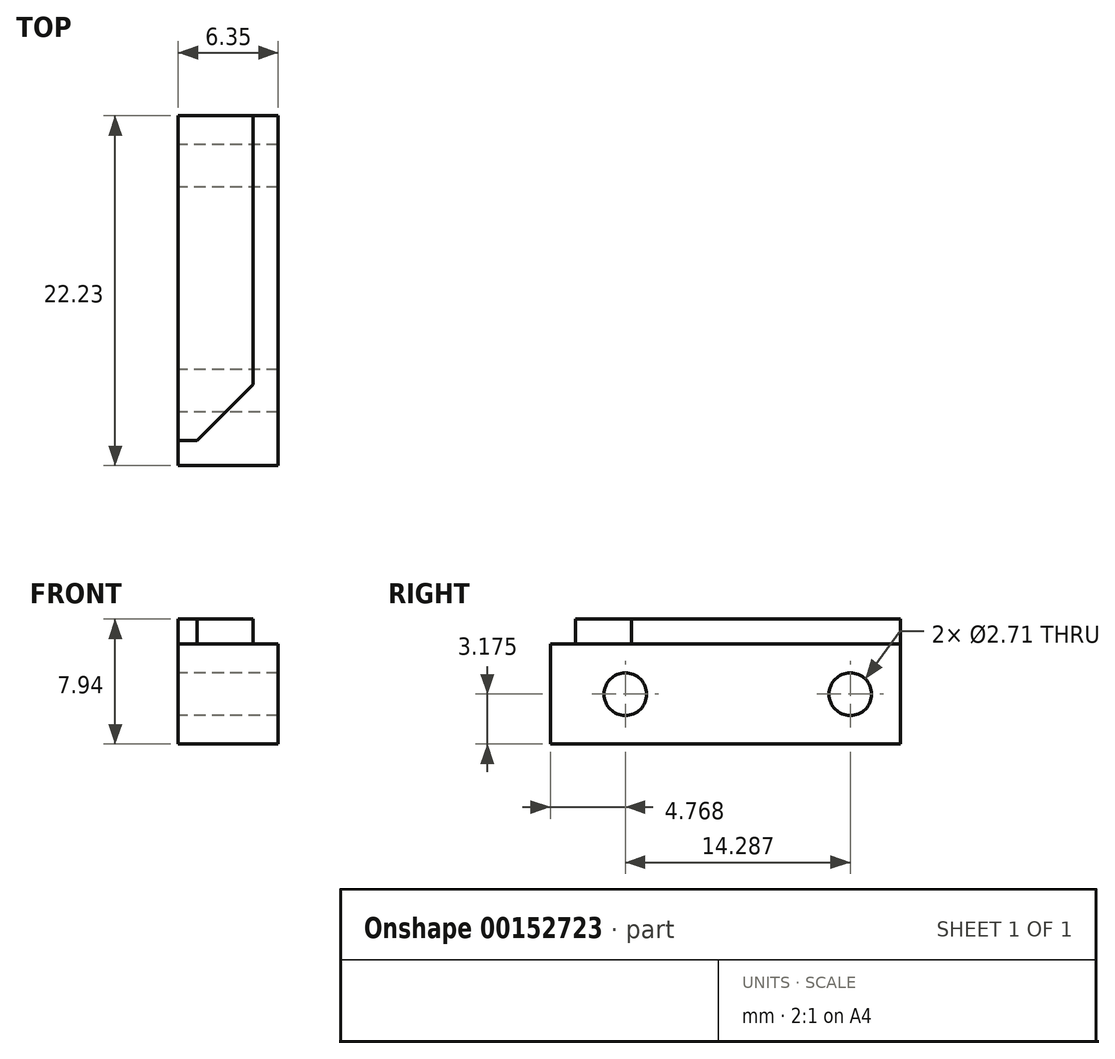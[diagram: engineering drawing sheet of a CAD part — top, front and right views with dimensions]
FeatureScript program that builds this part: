
annotation { "Feature Type Name" : "Feature", "Feature Type Description" : "" }
export const myFeature = defineFeature(function(context is Context, id is Id, definition is map)
    precondition{}
    {
        {
            var Q0;
            Q0=qCreatedBy(makeId("Top.planeOp"),FACE);
            var sketch = newSketch(context, id + "F0", { "sketchPlane" : qUnion([Q0])});
            skLineSegment(sketch, "E0.bottom", {"start": v(0, 0) * mm, "end": v(6.35, 0) * mm});
            skLineSegment(sketch, "E0.top", {"start": v(0, -22.23) * mm, "end": v(6.35, -22.23) * mm});
            skLineSegment(sketch, "E0.left", {"start": v(0, 0) * mm, "end": v(0, -22.23) * mm});
            skLineSegment(sketch, "E0.right", {"start": v(6.35, 0) * mm, "end": v(6.35, -22.23) * mm});
            skSolve(sketch);
        }
        {
            var Q0;
            Q0 = qSketchRegion(id + "F0", true);
            extrude(context, id + "F1", {"entities" : qUnion([Q0]), "depth" : 6.35 * mm});
        }
        {
            var Q0;
            Q0=makeQuery(id+"F1.opExtrude","CAP_FACE",FACE,{"disambiguationData":[OSD([sQuery(id+"F0.wireOp",EDGE,"E0.bottom"),sQuery(id+"F0.wireOp",EDGE,"E0.top"),sQuery(id+"F0.wireOp",EDGE,"E0.left"),sQuery(id+"F0.wireOp",EDGE,"E0.right")])],"isStart":false});
            var sketch = newSketch(context, id + "F2", { "sketchPlane" : qUnion([Q0])});
            skLineSegment(sketch, "E1.bottom", {"start": v(0, 0) * mm, "end": v(4.76, 0) * mm});
            skLineSegment(sketch, "E1.top", {"start": v(0, -20.64) * mm, "end": v(4.76, -20.64) * mm});
            skLineSegment(sketch, "E1.left", {"start": v(0, 0) * mm, "end": v(0, -20.64) * mm});
            skLineSegment(sketch, "E1.right", {"start": v(4.76, 0) * mm, "end": v(4.76, -20.64) * mm});
            skLineSegment(sketch, "E2.bottom", {"start": v(4.76, -20.64) * mm, "end": v(6.35, -20.64) * mm, "construction": true});
            skLineSegment(sketch, "E2.top", {"start": v(4.76, -22.23) * mm, "end": v(6.35, -22.23) * mm, "construction": true});
            skLineSegment(sketch, "E2.left", {"start": v(4.76, -20.64) * mm, "end": v(4.76, -22.23) * mm, "construction": true});
            skLineSegment(sketch, "E2.right", {"start": v(6.35, -20.64) * mm, "end": v(6.35, -22.23) * mm, "construction": true});
            skSolve(sketch);
        }
        {
            var Q0;
            Q0 = qSketchRegion(id + "F2", true);
            extrude(context, id + "F3", {"entities" : qUnion([Q0]), "operationType" : NewBodyOperationType.ADD, "depth" : 1.59 * mm});
        }
        {
            var Q0;
            Q0=makeQuery(id+"F3.boolean.opBoolean","MERGE",FACE,{"derivedFrom":[makeQuery(id+"F1.opExtrude","SWEPT_FACE",FACE,{"disambiguationData":[OSD([sQuery(id+"F0.wireOp",EDGE,"E0.left")])]}),makeQuery(id+"F3.opExtrude","SWEPT_FACE",FACE,{"disambiguationData":[OSD([sQuery(id+"F2.wireOp",EDGE,"E1.left")])]})]});
            var sketch = newSketch(context, id + "F4", { "sketchPlane" : qUnion([Q0])});
            skLineSegment(sketch, "E3", {"start": v(20.64, 3.18) * mm, "end": v(17.46, 3.17) * mm, "construction": true});
            skLineSegment(sketch, "E4", {"start": v(3.17, 3.17) * mm, "end": v(0, 3.17) * mm, "construction": true});
            skCircle(sketch, "E5", {"center": v(17.46, 3.18) * mm, "radius": 1.35 * mm});
            skCircle(sketch, "E6", {"center": v(3.17, 3.17) * mm, "radius": 1.35 * mm});
            skLineSegment(sketch, "E7", {"start": v(20.64, 3.17) * mm, "end": v(20.64, 6.35) * mm, "construction": true});
            skSolve(sketch);
        }
        {
            var Q0;
            Q0 = qSketchRegion(id + "F4", true);
            extrude(context, id + "F5", {"entities" : qUnion([Q0]), "operationType" : NewBodyOperationType.REMOVE, "oppositeDirection" : true, "depth" : 6.35 * mm});
        }
        {
            var Q0;
            Q0=makeQuery(id+"F3.opExtrude","SWEPT_EDGE",EDGE,{"disambiguationData":[OSD([sQuery(id+"F2.wireOp",EDGE,"E1.top"),sQuery(id+"F2.wireOp",EDGE,"E1.right")])]});
            chamfer(context, id + "F6", {"entities" : qUnion([Q0]), "width" : 3.57 * mm, "tangentPropagation" : true});
        }
    });
